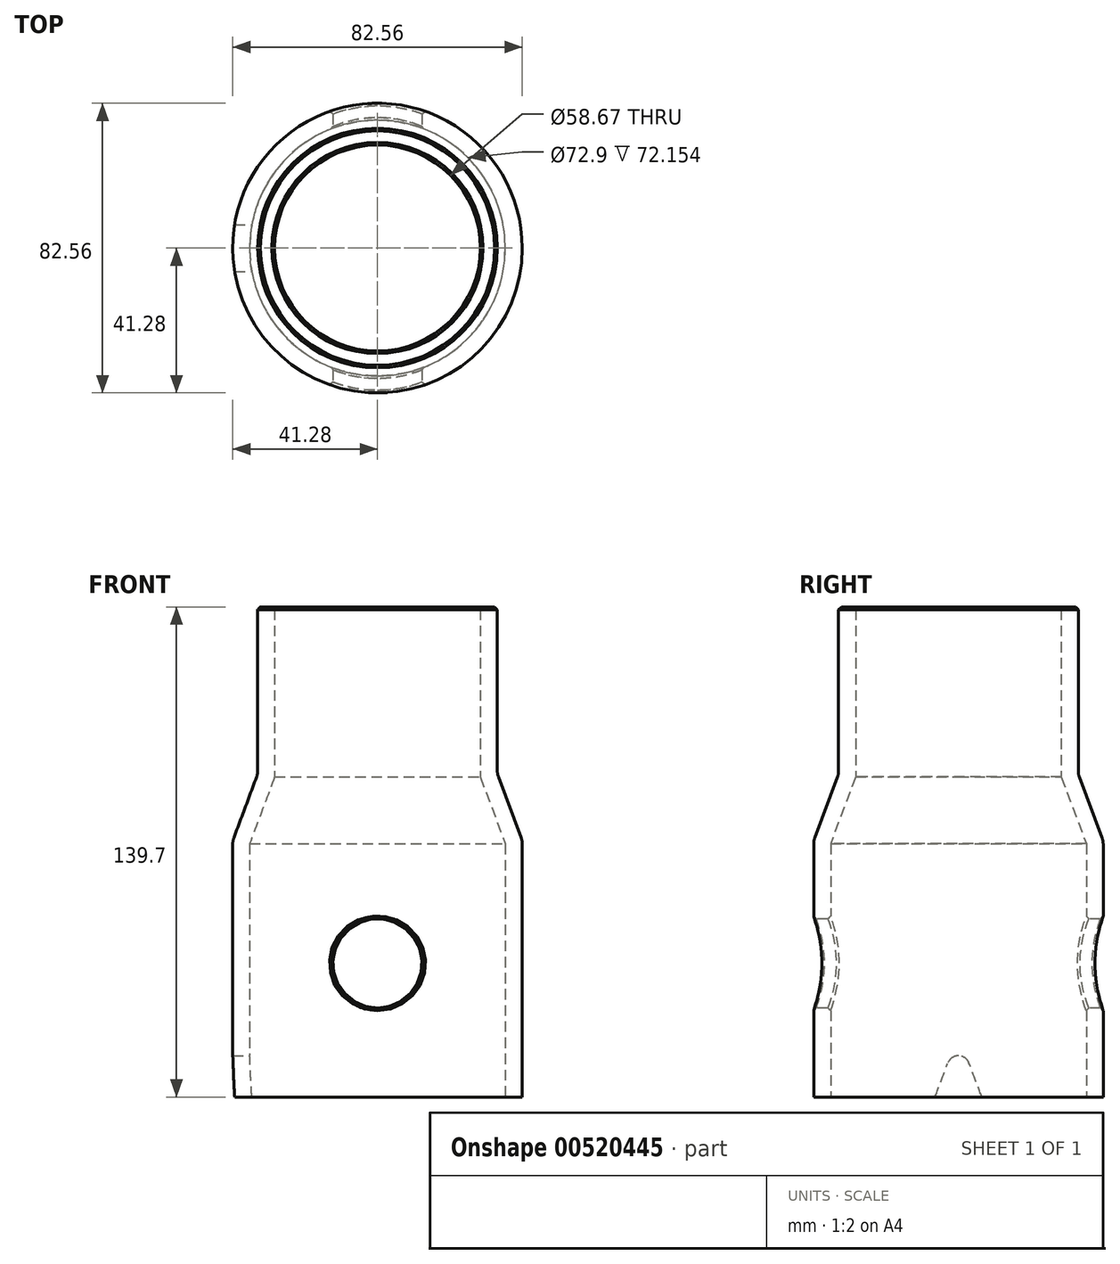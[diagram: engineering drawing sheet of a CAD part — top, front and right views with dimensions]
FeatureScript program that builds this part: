
annotation { "Feature Type Name" : "Feature", "Feature Type Description" : "" }
export const myFeature = defineFeature(function(context is Context, id is Id, definition is map)
    precondition{}
    {
        {
            var Q0;
            Q0=qCreatedBy(makeId("Front.planeOp"),FACE);
            var sketch = newSketch(context, id + "F0", { "sketchPlane" : qUnion([Q0])});
            skLineSegment(sketch, "E0", {"start": v(-34.16, 139.7) * mm, "end": v(-34.16, 92.08) * mm});
            skLineSegment(sketch, "E1", {"start": v(-34.16, 92.08) * mm, "end": v(-41.28, 73.02) * mm});
            skLineSegment(sketch, "E2", {"start": v(-41.28, 73.03) * mm, "end": v(-41.27, 0) * mm});
            skLineSegment(sketch, "E3", {"start": v(-41.27, 0) * mm, "end": v(0, 0) * mm});
            skLineSegment(sketch, "E4", {"start": v(0, 0) * mm, "end": v(0, 139.7) * mm});
            skLineSegment(sketch, "E5", {"start": v(0, 139.7) * mm, "end": v(-34.16, 139.7) * mm});
            skSolve(sketch);
        }
        {
            var Q0;
            Q0 = qSketchRegion(id + "F0", true);
            var Q1;
            Q1=sQuery(id+"F0.wireOp",EDGE,"E4");
            revolve(context, id + "F1", {"entities" : qUnion([Q0]), "axis" : qUnion([Q1]), "revolveType" : RevolveType.FULL});
        }
        {
            var Q0;
            Q0=makeQuery(id+"F1.opRevolve","SWEPT_FACE",FACE,{"disambiguationData":[OSD([sQuery(id+"F0.wireOp",EDGE,"E3")])]});
            var Q1;
            Q1=makeQuery(id+"F1.opRevolve","SWEPT_FACE",FACE,{"disambiguationData":[OSD([sQuery(id+"F0.wireOp",EDGE,"E5")])]});
            shell(context, id + "F2", {"entities" : qUnion([Q0, Q1]), "thickness" : 4.83 * mm});
        }
        {
            var Q0;
            Q0=qCreatedBy(makeId("Front.planeOp"),FACE);
            var sketch = newSketch(context, id + "F3", { "sketchPlane" : qUnion([Q0])});
            skCircle(sketch, "E6", {"center": v(0, 38.1) * mm, "radius": 12.7 * mm});
            skSolve(sketch);
        }
        {
            var Q0;
            Q0 = qSketchRegion(id + "F3", true);
            extrude(context, id + "F4", {"entities" : qUnion([Q0]), "operationType" : NewBodyOperationType.REMOVE, "endBound" : BoundingType.THROUGH_ALL, "oppositeDirection" : true, "depth" : 25.4 * mm, "offsetDistance" : 25.4 * mm, "hasSecondDirection" : true, "secondDirectionBound" : SecondDirectionBoundingType.THROUGH_ALL, "secondDirectionOppositeDirection" : false, "secondDirectionDepth" : 25.4 * mm});
        }
        {
            var Q0;
            Q0=makeQuery(id+"F2.opShell","OFFSET_EDGE",EDGE,{"disambiguationData":[OSD([sQuery(id+"F0.wireOp",EDGE,"E0"),sQuery(id+"F0.wireOp",EDGE,"E5")])]});
            var Q1;
            Q1=makeQuery(id+"F1.opRevolve","SWEPT_EDGE",EDGE,{"disambiguationData":[OSD([sQuery(id+"F0.wireOp",EDGE,"E0"),sQuery(id+"F0.wireOp",EDGE,"E5")])]});
            var Q2;
            Q2=makeQuery(id+"F4.boolean.opBoolean","INTERSECT",EDGE,{"disambiguationData":[OD(0.0)],"derivedFrom":[makeQuery(id+"F2.opShell","OFFSET_FACE",FACE,{"disambiguationData":[OSD([sQuery(id+"F0.wireOp",EDGE,"E2")])]}),makeQuery(id+"F4.opExtrude","SWEPT_FACE",FACE,{"disambiguationData":[OSD([sQuery(id+"F3.wireOp",EDGE,"E6")])]})]});
            var Q3;
            Q3=makeQuery(id+"F4.boolean.opBoolean","INTERSECT",EDGE,{"disambiguationData":[OD(1.0)],"derivedFrom":[makeQuery(id+"F2.opShell","OFFSET_FACE",FACE,{"disambiguationData":[OSD([sQuery(id+"F0.wireOp",EDGE,"E2")])]}),makeQuery(id+"F4.opExtrude","SWEPT_FACE",FACE,{"disambiguationData":[OSD([sQuery(id+"F3.wireOp",EDGE,"E6")])]})]});
            var Q4;
            Q4=makeQuery(id+"F4.boolean.opBoolean","INTERSECT",EDGE,{"disambiguationData":[OD(1.0)],"derivedFrom":[makeQuery(id+"F1.opRevolve","SWEPT_FACE",FACE,{"disambiguationData":[OSD([sQuery(id+"F0.wireOp",EDGE,"E2")])]}),makeQuery(id+"F4.opExtrude","SWEPT_FACE",FACE,{"disambiguationData":[OSD([sQuery(id+"F3.wireOp",EDGE,"E6")])]})]});
            var Q5;
            Q5=makeQuery(id+"F4.boolean.opBoolean","INTERSECT",EDGE,{"disambiguationData":[OD(0.0)],"derivedFrom":[makeQuery(id+"F1.opRevolve","SWEPT_FACE",FACE,{"disambiguationData":[OSD([sQuery(id+"F0.wireOp",EDGE,"E2")])]}),makeQuery(id+"F4.opExtrude","SWEPT_FACE",FACE,{"disambiguationData":[OSD([sQuery(id+"F3.wireOp",EDGE,"E6")])]})]});
            chamfer(context, id + "F5", {"entities" : qUnion([Q0, Q1, Q2, Q3, Q4, Q5]), "width" : 0.76 * mm, "tangentPropagation" : true});
        }
        {
            var Q0;
            Q0=makeQuery(id+"F1.opRevolve","SWEPT_EDGE",EDGE,{"disambiguationData":[OSD([sQuery(id+"F0.wireOp",EDGE,"E1"),sQuery(id+"F0.wireOp",EDGE,"E2")])]});
            var Q1;
            Q1=makeQuery(id+"F1.opRevolve","SWEPT_EDGE",EDGE,{"disambiguationData":[OSD([sQuery(id+"F0.wireOp",EDGE,"E0"),sQuery(id+"F0.wireOp",EDGE,"E1")])]});
            fillet(context, id + "F6", {"entities" : qUnion([Q0, Q1]), "radius" : 5.08 * mm, "tangentPropagation" : true, "allowEdgeOverflow" : false});
        }
        {
            var Q0;
            Q0=qCreatedBy(makeId("Right.planeOp"),FACE);
            var sketch = newSketch(context, id + "F7", { "sketchPlane" : qUnion([Q0])});
            skArc(sketch, "E7", {"start": v(3.05, 9.64) * mm, "mid": v(0, 11.76) * mm, "end": v(-3.05, 9.64) * mm});
            skLineSegment(sketch, "E8", {"start": v(6.66, 0) * mm, "end": v(3.05, 9.64) * mm});
            skLineSegment(sketch, "E9.MirrorCS", {"start": v(-6.66, 0) * mm, "end": v(-3.05, 9.64) * mm});
            skLineSegment(sketch, "E10", {"start": v(-6.66, 0) * mm, "end": v(6.66, 0) * mm});
            skPoint(sketch, "E11.orphan", {"position": v(2.51, 11.08) * mm});
            skPoint(sketch, "E12.orphan", {"position": v(-2.51, 11.08) * mm});
            skSolve(sketch);
        }
        {
            var Q0;
            Q0=makeQuery(id+"F7.imprint","IMPRINT",FACE,{"disambiguationData":[TD([[makeQuery(id+"F7.imprint","IMPRINT",EDGE,{"derivedFrom":sQuery(id+"F7.wireOp",EDGE,"E7")}),1.0]])]});
            extrude(context, id + "F8", {"entities" : qUnion([Q0]), "operationType" : NewBodyOperationType.REMOVE, "endBound" : BoundingType.THROUGH_ALL, "oppositeDirection" : true, "depth" : 25.4 * mm, "offsetDistance" : 25.4 * mm});
        }
    });
